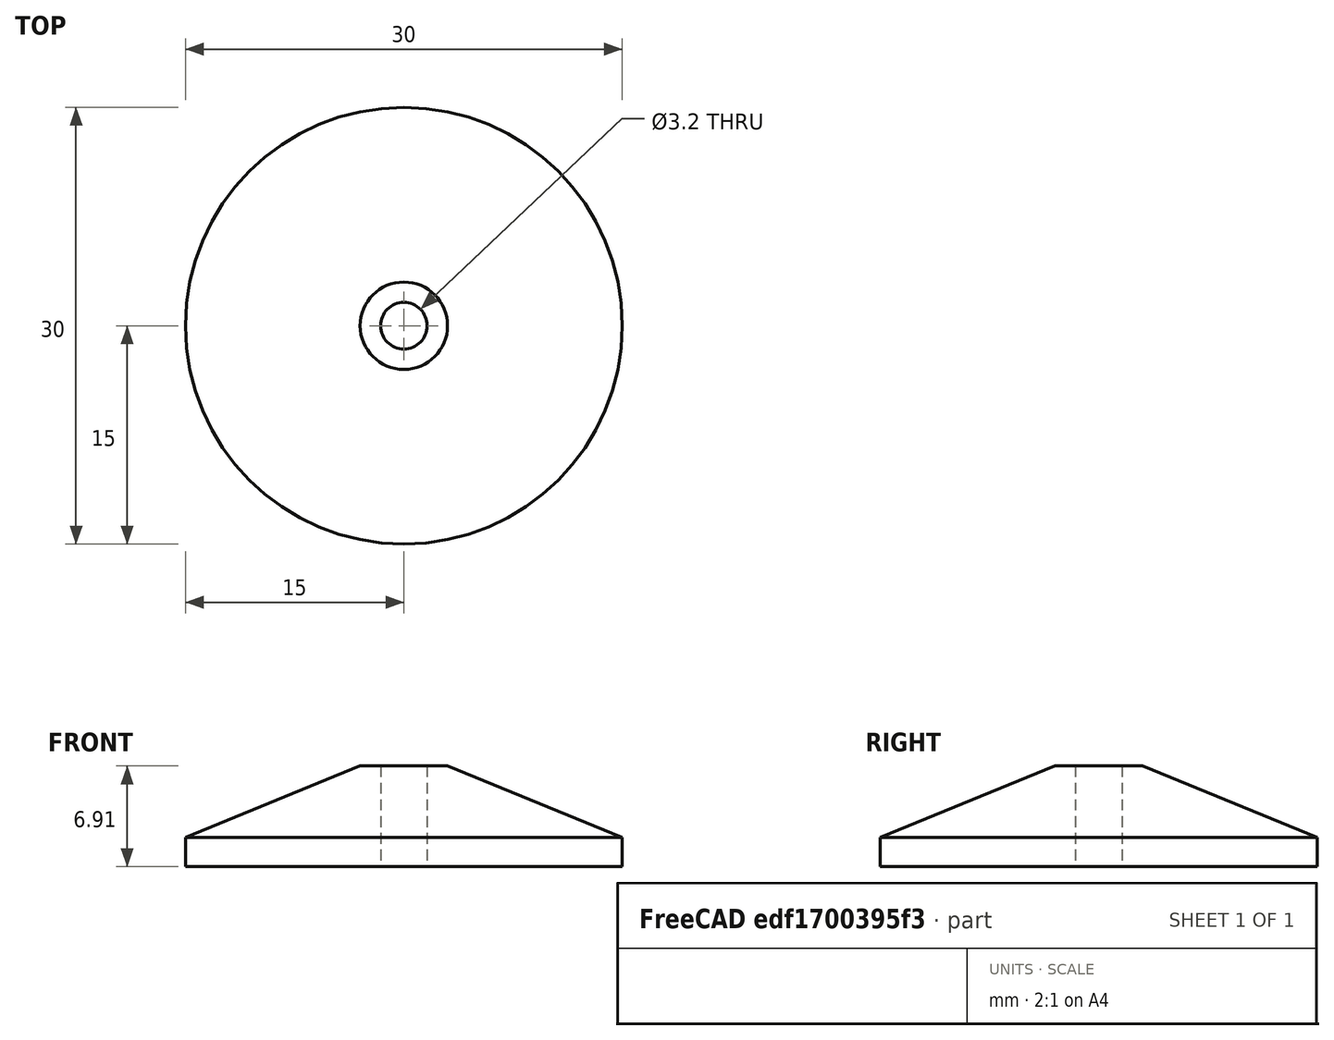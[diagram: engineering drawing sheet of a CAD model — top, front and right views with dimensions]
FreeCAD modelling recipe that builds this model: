
FCSTD DOCUMENT  (FreeCAD 0.17R13522 (Git))
Label: BobbinSocket_Small_R_A2
License: All rights reserved
LicenseURL: http://en.wikipedia.org/wiki/All_rights_reserved
objects: Sketcher::SketchObject×1, PartDesign::Revolution×1, PartDesign::Body×1, App::Part×1
note: 4 computed .brp shape members not serialized (recipe doc carries the construction recipe); baked Part::Feature solids carry a one-line shape summary decoded from their .brp

FEATURE [Sketcher::SketchObject] Sketch002
  MapMode = 5
  Placement = pos=(0,0,0) rot=(0.57735,0.57735,0.57735;2.0944rad)
  Support = -> [YZ_Plane001]
  sketch-geometry (5):
    g0: LineSegment StartX=1.6 StartY=6.90933 StartZ=0 EndX=1.6 EndY=0 EndZ=0
    g1: LineSegment StartX=15 StartY=0 StartZ=0 EndX=15 EndY=2 EndZ=0
    g2: LineSegment StartX=1.6 StartY=0 StartZ=0 EndX=15 EndY=0 EndZ=0
    g3: LineSegment StartX=1.6 StartY=6.90933 StartZ=0 EndX=3 EndY=6.90933 EndZ=0
    g4: LineSegment StartX=3 StartY=6.90933 StartZ=0 EndX=15 EndY=2 EndZ=0
  constraints (15):
    c: PointOnObject(g1,g-1)
    c: Vertical(g1)
    c: DistanceX(g-1,g0) = 1.6
    c: Vertical(g0)
    c: PointOnObject(g2,g-1)
    c: Coincident(g2,g1)
    c: DistanceX(g-1,g1) = 15
    c: Coincident(g0,g3)
    c: Horizontal(g3)
    c: Coincident(g3,g4)
    c: Coincident(g4,g1)
    c: DistanceX(g-1,g3) = 3
    c: Angle(g4,g2) = 0.388336
    c: Coincident(g2,g0)
    c: DistanceY(g1,g1) = 2
FEATURE [PartDesign::Revolution] Revolution
  Angle = 360
  Axis = (0,0,1)
  Base = (0,0,0)
  Placement = pos=(0,0,0) rot=(0.57735,0.57735,0.57735;2.0944rad)
  Profile = -> Sketch002
  ReferenceAxis = -> Sketch002 [V_Axis]
  Reversed = true
FEATURE [PartDesign::Body] RevolutionBody
  Group = -> [Sketch002,Revolution]
  Origin = -> Origin001
  Tip = -> Revolution
FEATURE [App::Part] Part
  Group = -> [RevolutionBody]
  License = CC BY 3.0
  LicenseURL = http://creativecommons.org/licenses/by/3.0/
  Origin = -> Origin
